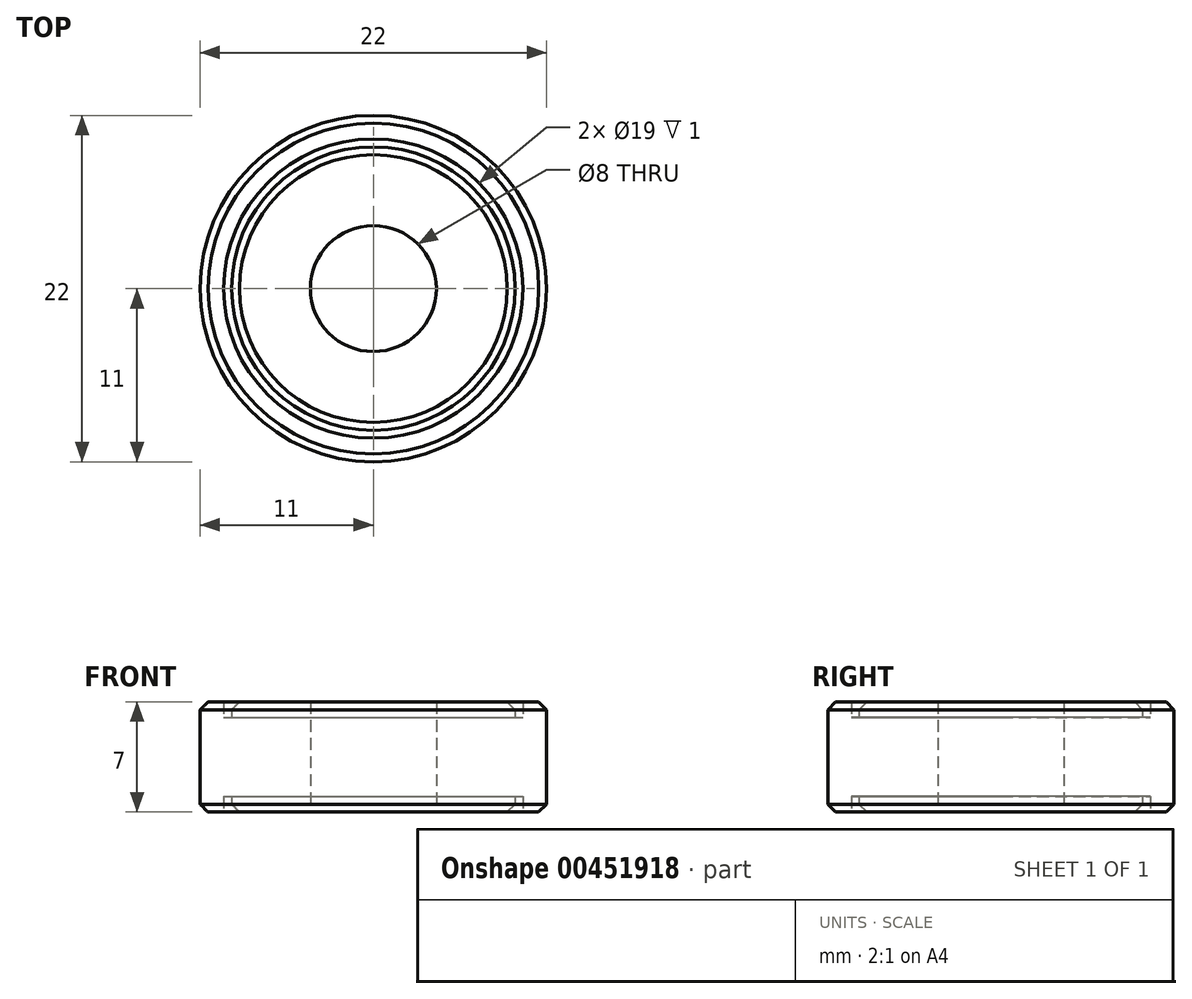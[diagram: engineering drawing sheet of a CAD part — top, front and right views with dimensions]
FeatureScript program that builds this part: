
annotation { "Feature Type Name" : "Feature", "Feature Type Description" : "" }
export const myFeature = defineFeature(function(context is Context, id is Id, definition is map)
    precondition{}
    {
        {
            var Q0;
            Q0=qCreatedBy(makeId("Front.planeOp"),FACE);
            var sketch = newSketch(context, id + "F0", { "sketchPlane" : qUnion([Q0])});
            skLineSegment(sketch, "E0", {"start": v(0, 2.89) * mm, "end": v(0, -5.57) * mm, "construction": true});
            skLineSegment(sketch, "E1", {"start": v(-4, 0) * mm, "end": v(-4, 3.5) * mm});
            skLineSegment(sketch, "E2", {"start": v(-4, 3.5) * mm, "end": v(-8.5, 3.5) * mm});
            skLineSegment(sketch, "E3", {"start": v(-8.5, 3.5) * mm, "end": v(-9, 3) * mm});
            skLineSegment(sketch, "E4", {"start": v(-9, 3) * mm, "end": v(-9, 2.5) * mm});
            skLineSegment(sketch, "E5", {"start": v(-9, 2.5) * mm, "end": v(-9.5, 2.5) * mm});
            skLineSegment(sketch, "E6", {"start": v(-9.5, 2.5) * mm, "end": v(-9.5, 3.5) * mm});
            skLineSegment(sketch, "E7", {"start": v(-9.5, 3.5) * mm, "end": v(-10.5, 3.5) * mm});
            skLineSegment(sketch, "E8", {"start": v(-10.5, 3.5) * mm, "end": v(-11, 3) * mm});
            skLineSegment(sketch, "E9", {"start": v(-11, 3) * mm, "end": v(-11, 0) * mm});
            skLineSegment(sketch, "E10", {"start": v(-4, 0) * mm, "end": v(-11, 0) * mm, "construction": true});
            skLineSegment(sketch, "E11.MirrorCS", {"start": v(-9, -3) * mm, "end": v(-9, -2.5) * mm});
            skLineSegment(sketch, "E12.MirrorCS", {"start": v(-8.5, -3.5) * mm, "end": v(-9, -3) * mm});
            skLineSegment(sketch, "E13.MirrorCS", {"start": v(-9, -2.5) * mm, "end": v(-9.5, -2.5) * mm});
            skLineSegment(sketch, "E14.MirrorCS", {"start": v(0, -2.89) * mm, "end": v(0, 5.57) * mm, "construction": true});
            skLineSegment(sketch, "E15.MirrorCS", {"start": v(-11, -3) * mm, "end": v(-11, 0) * mm});
            skLineSegment(sketch, "E16.MirrorCS", {"start": v(-4, -3.5) * mm, "end": v(-8.5, -3.5) * mm});
            skLineSegment(sketch, "E17.MirrorCS", {"start": v(-10.5, -3.5) * mm, "end": v(-11, -3) * mm});
            skLineSegment(sketch, "E18.MirrorCS", {"start": v(-9.5, -3.5) * mm, "end": v(-10.5, -3.5) * mm});
            skLineSegment(sketch, "E19.MirrorCS", {"start": v(-4, 0) * mm, "end": v(-4, -3.5) * mm});
            skLineSegment(sketch, "E20.MirrorCS", {"start": v(-9.5, -2.5) * mm, "end": v(-9.5, -3.5) * mm});
            skSolve(sketch);
        }
        {
            var Q0;
            Q0=qSketchRegion(id+"F0",true);
            var Q1;
            Q1=sQuery(id+"F0.wireOp",EDGE,"E14.MirrorCS");
            revolve(context, id + "F1", {"entities" : qUnion([Q0]), "axis" : qUnion([Q1]), "revolveType" : RevolveType.FULL});
        }
    });
